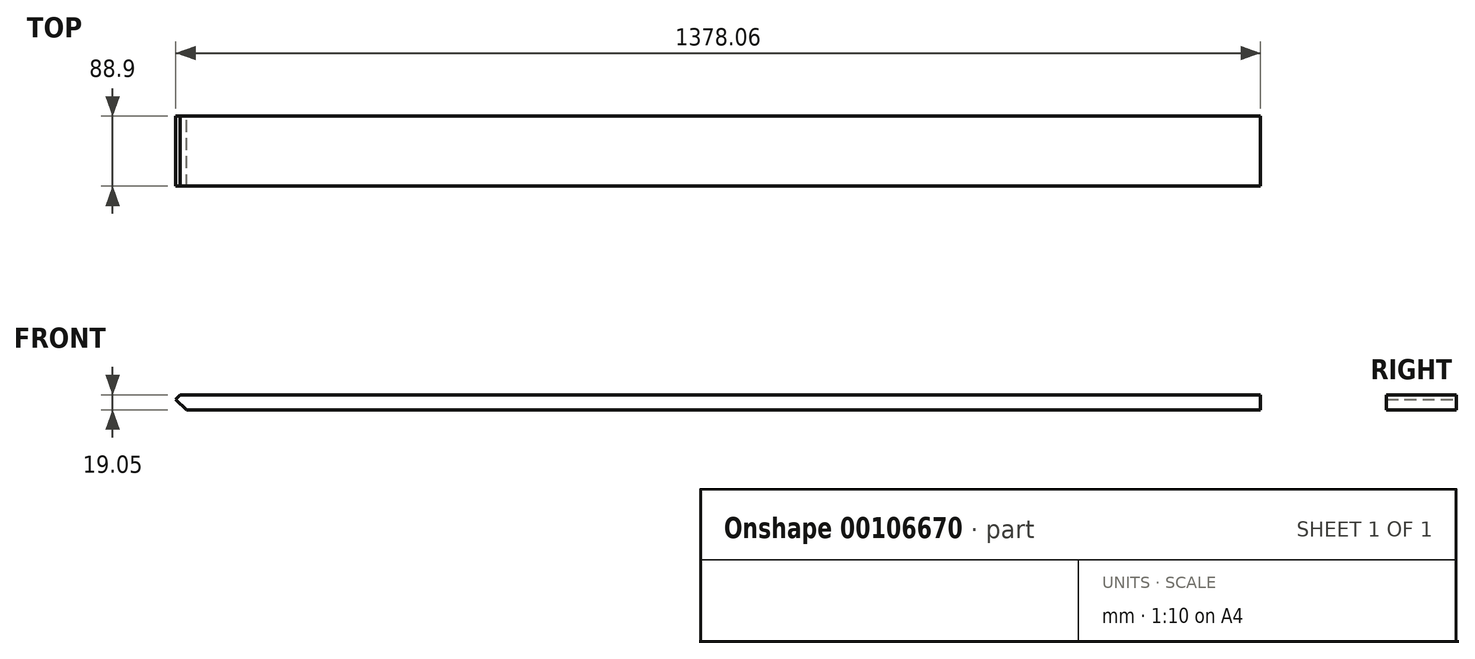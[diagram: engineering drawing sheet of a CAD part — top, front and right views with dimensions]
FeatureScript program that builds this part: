
annotation { "Feature Type Name" : "Feature", "Feature Type Description" : "" }
export const myFeature = defineFeature(function(context is Context, id is Id, definition is map)
    precondition{}
    {
        {
            var Q0;
            Q0=qCreatedBy(makeId("Front.planeOp"),FACE);
            var sketch = newSketch(context, id + "F0", { "sketchPlane" : qUnion([Q0])});
            skLineSegment(sketch, "E0.bottom", {"start": v(0, 0) * mm, "end": v(-1364.37, 0) * mm});
            skLineSegment(sketch, "E0.top", {"start": v(0, 19.05) * mm, "end": v(-1364.37, 19.05) * mm});
            skLineSegment(sketch, "E0.left", {"start": v(0, 0) * mm, "end": v(0, 19.05) * mm});
            skLineSegment(sketch, "E0.right", {"start": v(-1364.37, 0) * mm, "end": v(-1364.37, 19.05) * mm});
            skLineSegment(sketch, "E1", {"start": v(-1364.37, 0) * mm, "end": v(-1378.06, 13.25) * mm});
            skLineSegment(sketch, "E2", {"start": v(-1364.37, 19.05) * mm, "end": v(-1372.44, 19.05) * mm});
            skLineSegment(sketch, "E3", {"start": v(-1378.06, 13.25) * mm, "end": v(-1372.44, 19.05) * mm});
            skSolve(sketch);
        }
        {
            var Q0;
            Q0=makeQuery(id+"F0.imprint","IMPRINT",FACE,{"disambiguationData":[TD([[makeQuery(id+"F0.imprint","IMPRINT",EDGE,{"derivedFrom":sQuery(id+"F0.wireOp",EDGE,"E0.right")}),1.0]])]});
            var Q1;
            Q1=makeQuery(id+"F0.imprint","IMPRINT",FACE,{"disambiguationData":[TD([[makeQuery(id+"F0.imprint","IMPRINT",EDGE,{"derivedFrom":sQuery(id+"F0.wireOp",EDGE,"E0.bottom")}),-1.0]])]});
            extrude(context, id + "F1", {"entities" : qUnion([Q0, Q1]), "depth" : 88.9 * mm});
        }
    });
